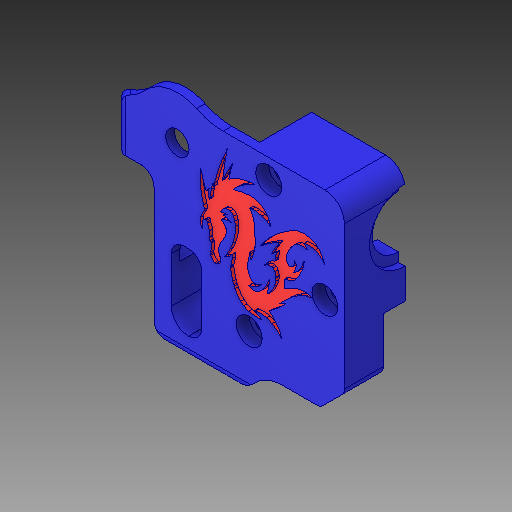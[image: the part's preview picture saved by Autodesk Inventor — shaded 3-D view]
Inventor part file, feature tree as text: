
AUTODESK INVENTOR PART (.ipt)
format: ipt  version: 2019 (Build 230136000, 136)  size: 2,478,080 bytes
history: native  units: mm
features: thicken_offset x10, fillet x2
ambient origin geometry x8: Origin, YZ Plane, XZ Plane, XY Plane, X Axis, Y Axis, Z Axis, Center Point
bodies: Solid1 (feature_tree)
feature tree (12):
  thicken_offset  "Thicken5"
  thicken_offset  "Thicken6"
  thicken_offset  "Thicken7"
  thicken_offset  "Thicken8"
  thicken_offset  "Thicken9"
  thicken_offset  "Thicken10"
  thicken_offset  "Thicken11"
  thicken_offset  "Thicken12"
  thicken_offset  "Thicken13"
  fillet  "Fillet1"  Radius=1.0mm
  thicken_offset  "Thicken14"
  fillet  "Fillet5"  Radius=1.0mm
